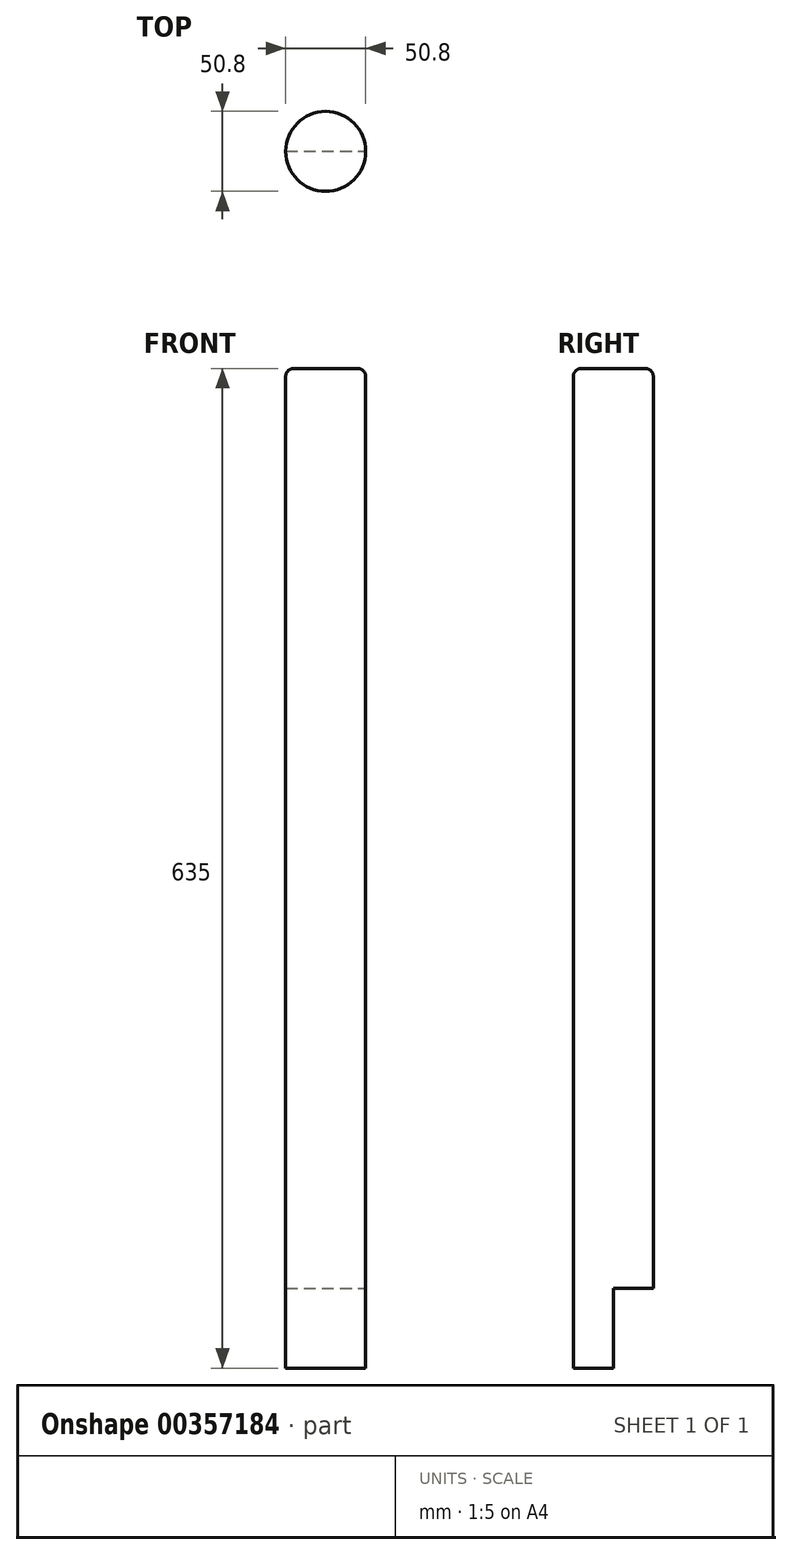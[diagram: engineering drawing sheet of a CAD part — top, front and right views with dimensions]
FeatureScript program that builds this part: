
annotation { "Feature Type Name" : "Feature", "Feature Type Description" : "" }
export const myFeature = defineFeature(function(context is Context, id is Id, definition is map)
    precondition{}
    {
        {
            var Q0;
            Q0=qCreatedBy(makeId("Top.planeOp"),FACE);
            var sketch = newSketch(context, id + "F0", { "sketchPlane" : qUnion([Q0])});
            skCircle(sketch, "E0", {"center": v(0, 0) * mm, "radius": 25.4 * mm});
            skSolve(sketch);
        }
        {
            var Q0;
            Q0 = qSketchRegion(id + "F0", true);
            extrude(context, id + "F1", {"entities" : qUnion([Q0]), "depth" : 635 * mm});
        }
        {
            var Q0;
            Q0=qCreatedBy(makeId("Front.planeOp"),FACE);
            var sketch = newSketch(context, id + "F2", { "sketchPlane" : qUnion([Q0])});
            skLineSegment(sketch, "E1.bottom", {"start": v(-31.57, 0) * mm, "end": v(31.93, 0) * mm});
            skLineSegment(sketch, "E1.top", {"start": v(-31.57, 50.8) * mm, "end": v(31.93, 50.8) * mm});
            skLineSegment(sketch, "E1.left", {"start": v(-31.57, 0) * mm, "end": v(-31.57, 50.8) * mm});
            skLineSegment(sketch, "E1.right", {"start": v(31.93, 0) * mm, "end": v(31.93, 50.8) * mm});
            skSolve(sketch);
        }
        {
            var Q0;
            Q0 = qSketchRegion(id + "F2", true);
            var Q1;
            Q1 = qConstructionFilter(qBodyType(qCreatedBy(id + "F2" ,EDGE), BodyType.WIRE), ConstructionObject.NO);
            extrude(context, id + "F3", {"entities" : qUnion([Q0]), "operationType" : NewBodyOperationType.REMOVE, "surfaceEntities" : qUnion([Q1]), "oppositeDirection" : true, "depth" : 25.4 * mm});
        }
        {
            var Q0;
            Q0=makeQuery(id+"F1.opExtrude","CAP_EDGE",EDGE,{"disambiguationData":[OSD([sQuery(id+"F0.wireOp",EDGE,"E0")])],"isStart":false});
            fillet(context, id + "F4", {"entities" : qUnion([Q0]), "radius" : 5.08 * mm, "tangentPropagation" : true, "allowEdgeOverflow" : false});
        }
    });
